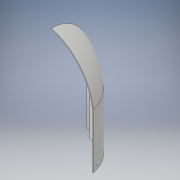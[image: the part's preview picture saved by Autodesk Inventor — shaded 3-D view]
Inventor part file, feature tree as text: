
AUTODESK INVENTOR PART (.ipt)
format: ipt  version: 2019 (Build 230136000, 136)  size: 310,784 bytes
history: native  units: mm
features: sketch x7, extrude x4, other x3, loft x1, shell x1, projected_geometry x1
ambient origin geometry x8: Origin, YZ Plane, XZ Plane, XY Plane, X Axis, Y Axis, Z Axis, Center Point
bodies: Body1 (feature_tree)
feature tree (17):
  other  "правое надкрылье"
  sketch  "Эскиз3"
  sketch  "Эскиз4"
  other  "РабПлоскость1"
  loft  "Лофт1"
  extrude  "Выдавливание2"  Depth=100.0mm
  shell  "Оболочка1"  Thickness=17.0mm
  extrude  "Выдавливание3"  Depth=4.0mm
  extrude  "Выдавливание6"  Depth=35.0mm
  other  "РабПлоскость2"
  extrude  "Выдавливание7"  TaperAngle=0.0deg  [1 undecoded]
  sketch  "Эскиз5"
  sketch  "Эскиз6"
  projected_geometry  "Спроецированная петля1"
  sketch  "Эскиз7"
  sketch  "Эскиз10"
  sketch  "Эскиз11"
note: 1 required parameter value undecoded (feature->parameter linkage not recoverable at this tier; creation-order binding heuristic only, values carry confidence <= 0.55)
